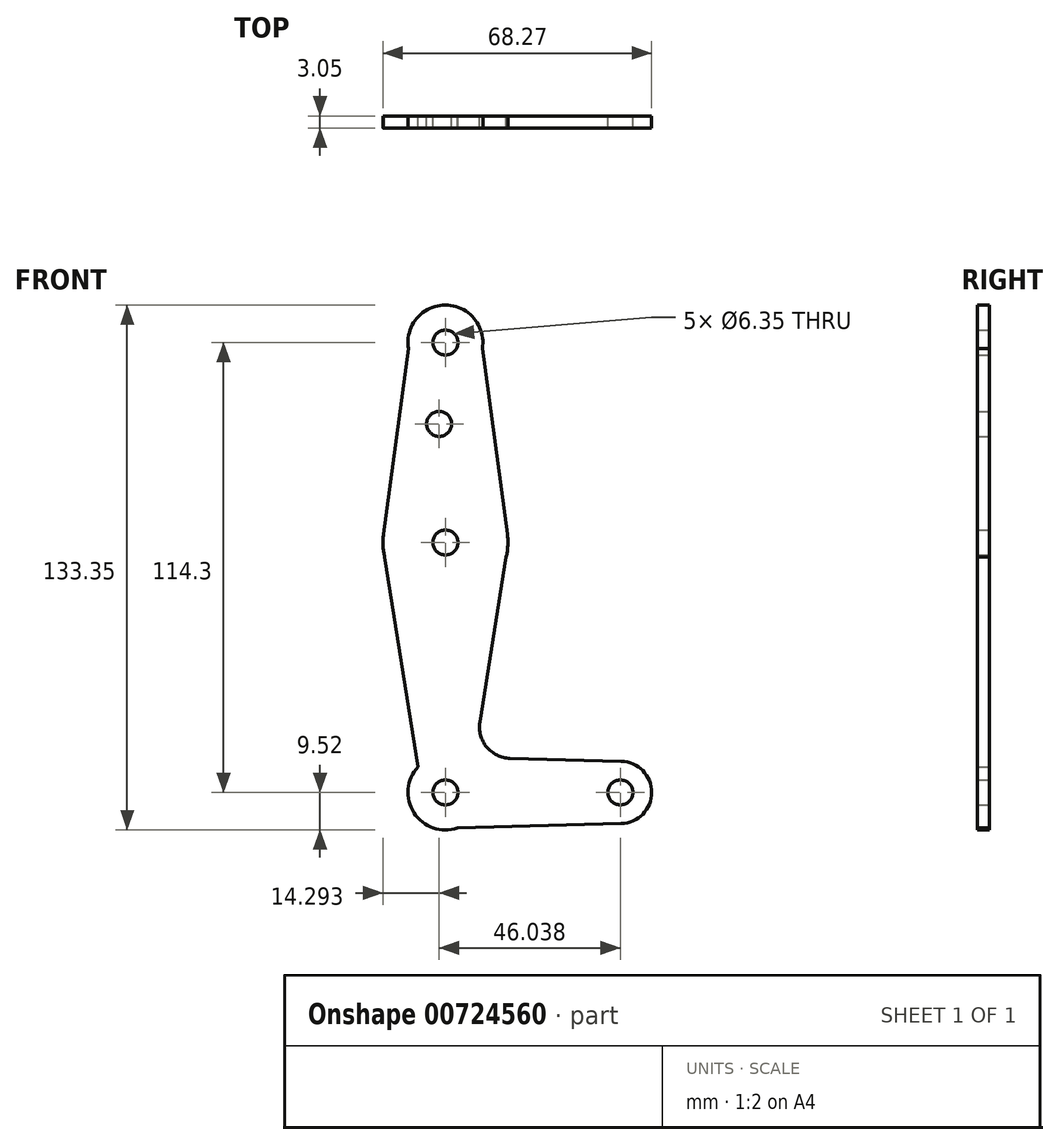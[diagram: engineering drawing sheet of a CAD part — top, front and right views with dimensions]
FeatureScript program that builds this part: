
annotation { "Feature Type Name" : "Feature", "Feature Type Description" : "" }
export const myFeature = defineFeature(function(context is Context, id is Id, definition is map)
    precondition{}
    {
        {
            var Q0;
            Q0=qCreatedBy(makeId("Front.planeOp"),FACE);
            var sketch = newSketch(context, id + "F0", { "sketchPlane" : qUnion([Q0])});
            skLineSegment(sketch, "E0", {"start": v(0, 0) * mm, "end": v(0, 114.3) * mm, "construction": true});
            skLineSegment(sketch, "E1", {"start": v(0, 0) * mm, "end": v(44.45, 0) * mm, "construction": true});
            skCircle(sketch, "E2", {"center": v(0, 114.3) * mm, "radius": 9.53 * mm});
            skCircle(sketch, "E3", {"center": v(0, 0) * mm, "radius": 9.53 * mm});
            skCircle(sketch, "E4", {"center": v(44.45, 0) * mm, "radius": 7.94 * mm});
            skCircle(sketch, "E5", {"center": v(0, 63.5) * mm, "radius": 15.88 * mm});
            skLineSegment(sketch, "E6", {"start": v(-9.4, 112.73) * mm, "end": v(-15.73, 65.62) * mm});
            skLineSegment(sketch, "E7", {"start": v(9.4, 112.73) * mm, "end": v(15.73, 65.62) * mm});
            skLineSegment(sketch, "E8", {"start": v(-15.43, 59.78) * mm, "end": v(-6.95, 6.51) * mm});
            skLineSegment(sketch, "E9", {"start": v(15.43, 59.78) * mm, "end": v(8.76, 17.87) * mm});
            skLineSegment(sketch, "E10", {"start": v(16.4, 8.67) * mm, "end": v(44.66, 7.93) * mm});
            skLineSegment(sketch, "E11", {"start": v(44.66, -7.93) * mm, "end": v(3.08, -9.01) * mm});
            skCircle(sketch, "E12", {"center": v(0, 114.3) * mm, "radius": 3.18 * mm});
            skCircle(sketch, "E13", {"center": v(0, 63.5) * mm, "radius": 3.18 * mm});
            skCircle(sketch, "E14", {"center": v(0, 0) * mm, "radius": 3.18 * mm});
            skCircle(sketch, "E15", {"center": v(44.45, 0) * mm, "radius": 3.18 * mm});
            skCircle(sketch, "E16", {"center": v(-1.59, 93.63) * mm, "radius": 3.18 * mm});
            skPoint(sketch, "E17.newPointA", {"position": v(6.95, 6.51) * mm});
            skArc(sketch, "E17.filletArc", {"start": v(8.76, 17.87) * mm, "mid": v(10.5, 11.53) * mm, "end": v(16.4, 8.67) * mm});
            skSolve(sketch);
        }
        {
            var Q0;
            Q0 = qSketchRegion(id + "F0", true);
            extrude(context, id + "F1", {"entities" : qUnion([Q0]), "depth" : 3.05 * mm, "offsetDistance" : 25.4 * mm});
        }
    });
